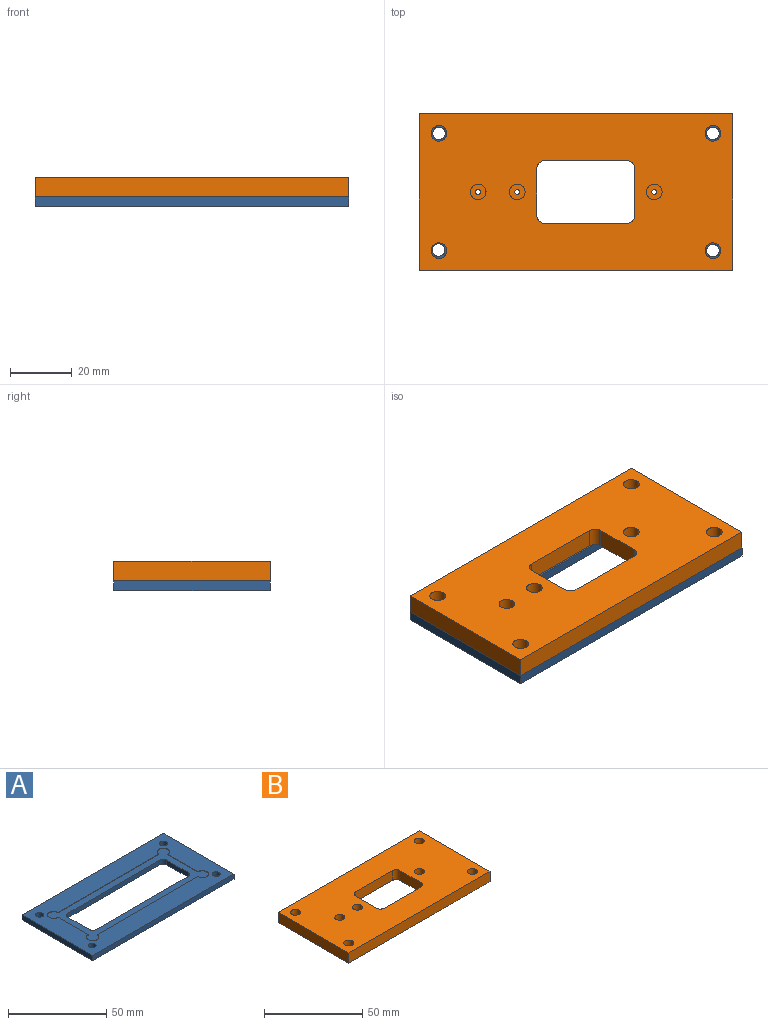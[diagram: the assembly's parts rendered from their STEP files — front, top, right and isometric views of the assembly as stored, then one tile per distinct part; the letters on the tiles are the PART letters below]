
ASSEMBLY  parts=2 mates=1
PART A: 27 faces, bbox 101.6x50.8x3.2 mm
  f0: plane 101.6x50.8mm, normal (0,0,-1), area 3669.8mm2, adj f3,f4,f5,f6,f15,f16,f17,f18
  f1: plane 85.09x34.29mm, normal (0,0,1), area 855.4mm2, adj f7,f8,f9,f10,f11,f12,f13,f14
  f2: plane 101.6x50.8mm, normal (0,0,1), area 2814.4mm2, adj f3,f4,f5,f6,f7,f8,f9,f10
  f3: plane 50.8x3.18mm, normal (-1,0,0), area 161.3mm2, adj f0,f2,f4,f6
  f4: plane 101.6x3.18mm, normal (0,-1,0), area 322.6mm2, adj f0,f2,f3,f5
  f5: plane 50.8x3.18mm, normal (1,0,0), area 161.3mm2, adj f0,f2,f4,f6
  f6: plane 101.6x3.18mm, normal (0,1,0), area 322.6mm2, adj f0,f2,f3,f5
  f7: plane 72.39x0.25mm, normal (0,-1,0), area 18.4mm2, adj f1,f2,f8,f14
  f8: cylinder r=3.17mm len=6.35mm, axis (0,0,1), area 3.8mm2, adj f1,f2,f7,f9
  f9: plane 21.59x0.25mm, normal (1,0,0), area 5.5mm2, adj f1,f2,f8,f10
  f10: cylinder r=3.17mm len=6.35mm, axis (0,0,1), area 3.8mm2, adj f1,f2,f9,f11
  f11: plane 72.39x0.25mm, normal (0,1,0), area 18.4mm2, adj f1,f2,f10,f12
  f12: cylinder r=3.17mm len=6.35mm, axis (0,0,1), area 3.8mm2, adj f1,f2,f11,f13
  f13: plane 21.59x0.25mm, normal (-1,0,0), area 5.5mm2, adj f1,f2,f12,f14
  f14: cylinder r=3.17mm len=6.35mm, axis (0,0,1), area 3.8mm2, adj f1,f2,f7,f13
  f15: plane 66.04x2.92mm, normal (0,-1,0), area 192.9mm2, adj f0,f1,f16,f22
  f16: cylinder r=2.54mm len=2.92mm, axis (0,0,1), area 11.7mm2, adj f0,f1,f15,f17
  f17: plane 15.24x2.92mm, normal (1,0,0), area 44.5mm2, adj f0,f1,f16,f18
  f18: cylinder r=2.54mm len=2.92mm, axis (0,0,1), area 11.7mm2, adj f0,f1,f17,f19
  f19: plane 66.04x2.92mm, normal (0,1,0), area 192.9mm2, adj f0,f1,f18,f20
  f20: cylinder r=2.54mm len=2.92mm, axis (0,0,1), area 11.7mm2, adj f0,f1,f19,f21
  f21: plane 15.24x2.92mm, normal (-1,0,0), area 44.5mm2, adj f0,f1,f20,f22
  f22: cylinder r=2.54mm len=2.92mm, axis (0,0,1), area 11.7mm2, adj f0,f1,f15,f21
  f23: cylinder r=2.03mm len=4.06mm, axis (0,0,1), area 40.5mm2, adj f0,f2
  f24: cylinder r=2.03mm len=4.06mm, axis (0,0,1), area 40.5mm2, adj f0,f2
  f25: cylinder r=2.03mm len=4.06mm, axis (0,0,1), area 40.5mm2, adj f0,f2
  f26: cylinder r=2.03mm len=4.06mm, axis (0,0,1), area 40.5mm2, adj f0,f2
PART B: 42 faces, bbox 101.6x50.8x6.4 mm
  f0: cylinder r=0.79mm len=1.59mm, axis (0,0,-1), area 3.8mm2, adj f27,f32
  f1: cylinder r=0.79mm len=1.59mm, axis (0,0,-1), area 3.8mm2, adj f25,f30
  f2: cylinder r=0.79mm len=1.59mm, axis (0,0,-1), area 3.8mm2, adj f23,f28
  f3: plane 101.6x50.8mm, normal (0,0,-1), area 2785.2mm2, adj f4,f5,f6,f7,f9,f10,f11,f12
  f4: plane 101.6x6.35mm, normal (0,1,0), area 645.2mm2, adj f3,f5,f7,f8
  f5: plane 50.8x6.35mm, normal (-1,0,0), area 322.6mm2, adj f3,f4,f6,f8
  f6: plane 101.6x6.35mm, normal (0,-1,0), area 645.2mm2, adj f3,f5,f7,f8
  f7: plane 50.8x6.35mm, normal (1,0,0), area 322.6mm2, adj f3,f4,f6,f8
  f8: plane 101.6x50.8mm, normal (0,0,1), area 4379.8mm2, adj f4,f5,f6,f7,f18,f19,f20,f21
  f9: plane 72.39x0.25mm, normal (0,1,0), area 18.4mm2, adj f3,f10,f16,f17
  f10: cylinder r=3.17mm len=6.35mm, axis (0,0,-1), area 3.8mm2, adj f3,f9,f11,f17
  f11: plane 21.59x0.25mm, normal (1,0,0), area 5.5mm2, adj f3,f10,f12,f17
  f12: cylinder r=3.17mm len=6.35mm, axis (0,0,-1), area 3.8mm2, adj f3,f11,f13,f17
  f13: plane 72.39x0.25mm, normal (0,-1,0), area 18.4mm2, adj f3,f12,f14,f17
  f14: cylinder r=3.17mm len=6.35mm, axis (0,0,-1), area 3.8mm2, adj f3,f13,f15,f17
  f15: plane 21.59x0.25mm, normal (-1,0,0), area 5.5mm2, adj f3,f14,f16,f17
  f16: cylinder r=3.17mm len=6.35mm, axis (0,0,-1), area 3.8mm2, adj f3,f9,f15,f17
  f17: plane 85.09x34.29mm, normal (0,0,-1), area 1601.9mm2, adj f9,f10,f11,f12,f13,f14,f15,f16
  f18: cylinder r=2.54mm len=6.35mm, axis (0,0,-1), area 101.3mm2, adj f3,f8
  f19: cylinder r=2.54mm len=6.35mm, axis (0,0,-1), area 101.3mm2, adj f3,f8
  f20: cylinder r=2.54mm len=6.35mm, axis (0,0,-1), area 101.3mm2, adj f3,f8
  f21: cylinder r=2.54mm len=6.35mm, axis (0,0,-1), area 101.3mm2, adj f3,f8
  f22: cylinder r=2.38mm len=4.76mm, axis (0,0,-1), area 7.6mm2, adj f17,f23
  f23: plane 4.76x4.76mm, normal (0,0,-1), area 15.8mm2, adj f2,f22
  f24: cylinder r=2.38mm len=4.76mm, axis (0,0,-1), area 7.6mm2, adj f17,f25
  f25: plane 4.76x4.76mm, normal (0,0,-1), area 15.8mm2, adj f1,f24
  f26: cylinder r=2.38mm len=4.76mm, axis (0,0,-1), area 7.6mm2, adj f17,f27
  f27: plane 4.76x4.76mm, normal (0,0,-1), area 15.8mm2, adj f0,f26
  f28: plane 5.08x5.08mm, normal (0,0,1), area 18.3mm2, adj f2,f29
  f29: cylinder r=2.54mm len=5.08mm, axis (0,0,1), area 77mm2, adj f8,f28
  f30: plane 5.08x5.08mm, normal (0,0,1), area 18.3mm2, adj f1,f31
  f31: cylinder r=2.54mm len=5.08mm, axis (0,0,1), area 77mm2, adj f8,f30
  f32: plane 5.08x5.08mm, normal (0,0,1), area 18.3mm2, adj f0,f33
  f33: cylinder r=2.54mm len=5.08mm, axis (0,0,1), area 77mm2, adj f8,f32
  f34: plane 26.67x6.1mm, normal (0,-1,0), area 162.6mm2, adj f8,f17,f35,f39
  f35: cylinder r=2.54mm len=6.1mm, axis (0,0,-1), area 24.3mm2, adj f8,f17,f34,f36
  f36: plane 15.24x6.1mm, normal (-1,0,0), area 92.9mm2, adj f8,f17,f35,f37
  f37: cylinder r=2.54mm len=6.1mm, axis (0,0,-1), area 24.3mm2, adj f8,f17,f36,f38
  f38: plane 26.67x6.1mm, normal (0,1,0), area 162.6mm2, adj f8,f17,f37,f40
  f39: cylinder r=2.54mm len=6.1mm, axis (0,0,-1), area 24.3mm2, adj f8,f17,f34,f41
  f40: cylinder r=2.54mm len=6.1mm, axis (0,0,-1), area 24.3mm2, adj f8,f17,f38,f41
  f41: plane 15.24x6.1mm, normal (1,0,0), area 92.9mm2, adj f8,f17,f39,f40
PLACE A t=(-1.96,2.73,-2.14)mm fixed
PLACE B t=(-1.78,2.53,1.03)mm
MATE fastened A.f2 <-> B.f3  axis (0,0,1) through (-1.78,2.53,1.03)mm
